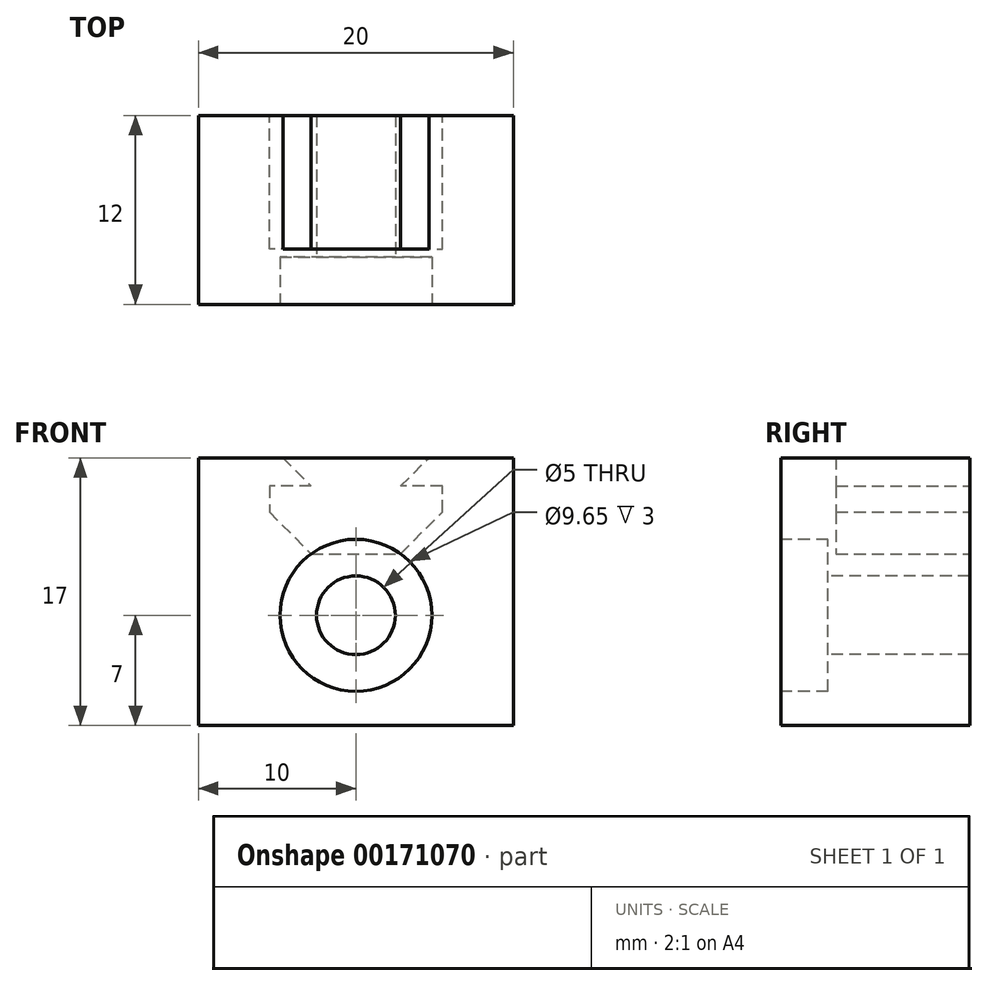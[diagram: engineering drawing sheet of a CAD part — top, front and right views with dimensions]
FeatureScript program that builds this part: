
annotation { "Feature Type Name" : "Feature", "Feature Type Description" : "" }
export const myFeature = defineFeature(function(context is Context, id is Id, definition is map)
    precondition{}
    {
        {
            var Q0;
            Q0=qCreatedBy(makeId("Front.planeOp"),FACE);
            var sketch = newSketch(context, id + "F0", { "sketchPlane" : qUnion([Q0])});
            skLineSegment(sketch, "E0", {"start": v(-10, -7) * mm, "end": v(-10, 10) * mm});
            skLineSegment(sketch, "E1", {"start": v(-4.64, 10) * mm, "end": v(-2.84, 8.2) * mm});
            skLineSegment(sketch, "E2", {"start": v(-2.84, 8.2) * mm, "end": v(-5.5, 8.2) * mm});
            skLineSegment(sketch, "E3", {"start": v(-5.5, 8.2) * mm, "end": v(-5.5, 6.56) * mm});
            skLineSegment(sketch, "E4", {"start": v(-5.5, 6.56) * mm, "end": v(-2.84, 3.9) * mm});
            skLineSegment(sketch, "E5", {"start": v(-2.84, 3.9) * mm, "end": v(2.84, 3.9) * mm});
            skLineSegment(sketch, "E6", {"start": v(2.84, 3.9) * mm, "end": v(5.5, 6.56) * mm});
            skLineSegment(sketch, "E7", {"start": v(5.5, 6.56) * mm, "end": v(5.5, 8.2) * mm});
            skLineSegment(sketch, "E8", {"start": v(5.5, 8.2) * mm, "end": v(2.84, 8.2) * mm});
            skLineSegment(sketch, "E9", {"start": v(2.84, 8.2) * mm, "end": v(4.64, 10) * mm});
            skLineSegment(sketch, "E10", {"start": v(10, 10) * mm, "end": v(10, -7) * mm});
            skPoint(sketch, "E11", {"position": v(0, 0) * mm});
            skLineSegment(sketch, "E12", {"start": v(-4.64, 10) * mm, "end": v(4.64, 10) * mm});
            skLineSegment(sketch, "E13", {"start": v(-10, 10) * mm, "end": v(10, 10) * mm});
            skLineSegment(sketch, "E14.0", {"start": v(10, -7) * mm, "end": v(-10, -7) * mm});
            skSolve(sketch);
        }
        {
            var Q0;
            {var subQ1=sQuery(id+"F0.wireOp",EDGE,"E0");Q0=makeQuery(id+"F0.imprint","IMPRINT",FACE,{"disambiguationData":[TD([[makeQuery(id+"F0.imprint","IMPRINT",EDGE,{"derivedFrom":subQ1}),-1.0]])]});}
            var Q1;
            {var subQ1=sQuery(id+"F0.wireOp",EDGE,"E1");Q1=makeQuery(id+"F0.imprint","IMPRINT",FACE,{"disambiguationData":[TD([[makeQuery(id+"F0.imprint","IMPRINT",EDGE,{"derivedFrom":subQ1}),1.0]])]});}
            extrude(context, id + "F1", {"entities" : qUnion([Q0, Q1]), "depth" : 12 * mm});
        }
        {
            var Q0;
            {var subQ1=sQuery(id+"F0.wireOp",EDGE,"E1");Q0=makeQuery(id+"F0.imprint","IMPRINT",FACE,{"disambiguationData":[TD([[makeQuery(id+"F0.imprint","IMPRINT",EDGE,{"derivedFrom":subQ1}),1.0]])]});}
            extrude(context, id + "F2", {"entities" : qUnion([Q0]), "operationType" : NewBodyOperationType.REMOVE, "depth" : 8.5 * mm});
        }
        {
            var Q0;
            Q0=makeQuery(id+"F1.opExtrude","CAP_FACE",FACE,{"disambiguationData":[OSD([sQuery(id+"F0.wireOp",EDGE,"E0"),sQuery(id+"F0.wireOp",EDGE,"E10"),sQuery(id+"F0.wireOp",EDGE,"851ea263-b1e6-4da8-9fdc-a8f08ad355ae"),sQuery(id+"F0.wireOp",EDGE,"E13")])],"isStart":false});
            var sketch = newSketch(context, id + "F3", { "sketchPlane" : qUnion([Q0])});
            skPoint(sketch, "E15", {"position": v(0, 0) * mm});
            skSolve(sketch);
        }
        {
            var Q0;
            Q0=sQuery(id+"F3.wireOp",VERTEX,"E15");
            var Q1;
            Q1=makeQuery(id+"F1.opExtrude","SWEPT_BODY",BODY,{"disambiguationData":[OSD([sQuery(id+"F0.wireOp",EDGE,"E0"),sQuery(id+"F0.wireOp",EDGE,"E10"),sQuery(id+"F0.wireOp",EDGE,"851ea263-b1e6-4da8-9fdc-a8f08ad355ae"),sQuery(id+"F0.wireOp",EDGE,"E13")])]});
            hole(context, id + "F4", {"style" : HoleStyle.C_BORE, "endStyle" : HoleEndStyle.THROUGH, "holeDiameter" : 5 * mm, "cBoreDiameter" : 9.65 * mm, "cBoreDepth" : 3 * mm, "tappedDepth" : 12 * mm, "tapClearance" : 3, "startFromSketch" : true, "locations" : qUnion([Q0]), "scope" : qUnion([Q1])});
        }
    });
